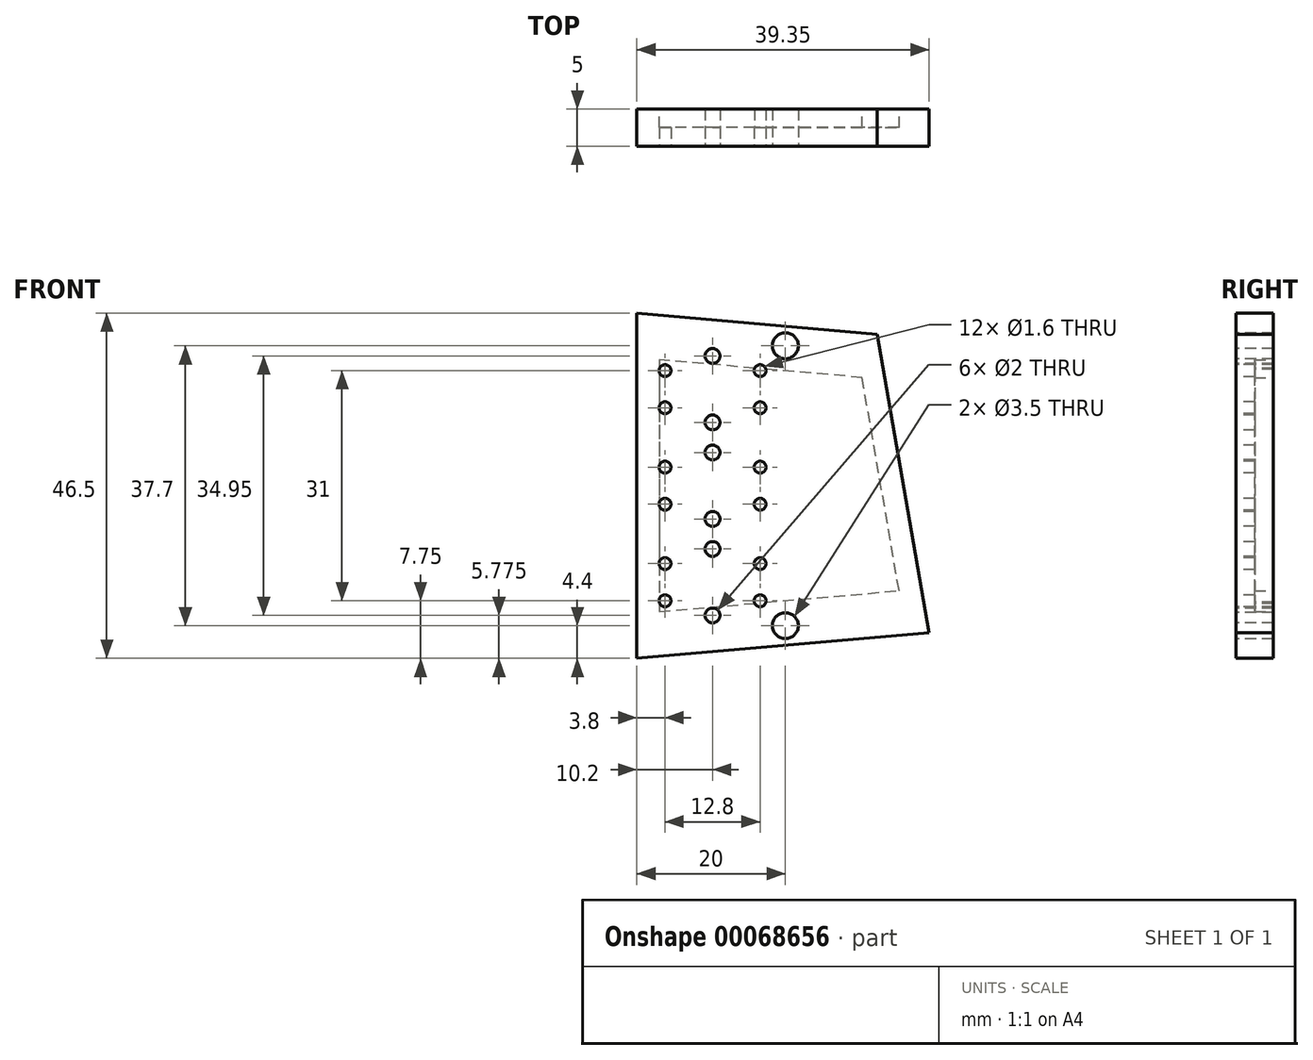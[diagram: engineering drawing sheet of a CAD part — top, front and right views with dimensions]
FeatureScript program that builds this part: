
annotation { "Feature Type Name" : "Feature", "Feature Type Description" : "" }
export const myFeature = defineFeature(function(context is Context, id is Id, definition is map)
    precondition{}
    {
        {
            var Q0;
            Q0=qCreatedBy(makeId("Front.planeOp"),FACE);
            var sketch = newSketch(context, id + "F0", { "sketchPlane" : qUnion([Q0])});
            skLineSegment(sketch, "E0", {"start": v(0, 46.5) * mm, "end": v(0, 0) * mm});
            skLineSegment(sketch, "E1", {"start": v(0, 0) * mm, "end": v(39.35, 3.44) * mm});
            skLineSegment(sketch, "E2", {"start": v(0, 46.5) * mm, "end": v(32.38, 43.67) * mm});
            skLineSegment(sketch, "E3", {"start": v(39.35, 3.44) * mm, "end": v(32.38, 43.67) * mm});
            skSolve(sketch);
        }
        {
            var Q0;
            Q0=makeQuery(id+"F0.imprint","IMPRINT",FACE,{"disambiguationData":[TD([[makeQuery(id+"F0.imprint","IMPRINT",EDGE,{"derivedFrom":sQuery(id+"F0.wireOp",EDGE,"E0")}),1.0]])]});
            extrude(context, id + "F1", {"entities" : qUnion([Q0]), "depth" : 5 * mm});
        }
        {
            var Q0;
            Q0=makeQuery(id+"F1.opExtrude","CAP_FACE",FACE,{"disambiguationData":[OSD([sQuery(id+"F0.wireOp",EDGE,"E0"),sQuery(id+"F0.wireOp",EDGE,"E1"),sQuery(id+"F0.wireOp",EDGE,"E2"),sQuery(id+"F0.wireOp",EDGE,"E3")])],"isStart":true});
            var sketch = newSketch(context, id + "F2", { "sketchPlane" : qUnion([Q0])});
            skLineSegment(sketch, "E4", {"start": v(-30.34, 37.82) * mm, "end": v(-3, 40.21) * mm});
            skLineSegment(sketch, "E5", {"start": v(-3, 40.21) * mm, "end": v(-3, 6.29) * mm});
            skLineSegment(sketch, "E6", {"start": v(-3, 6.29) * mm, "end": v(-35.32, 9.11) * mm});
            skLineSegment(sketch, "E7", {"start": v(-35.32, 9.11) * mm, "end": v(-30.34, 37.82) * mm});
            skSolve(sketch);
        }
        {
            var Q0;
            Q0=makeQuery(id+"F2.imprint","IMPRINT",FACE,{"disambiguationData":[TD([[makeQuery(id+"F2.imprint","IMPRINT",EDGE,{"derivedFrom":sQuery(id+"F2.wireOp",EDGE,"E4")}),-1.0]])]});
            extrude(context, id + "F3", {"entities" : qUnion([Q0]), "operationType" : NewBodyOperationType.REMOVE, "oppositeDirection" : true, "depth" : 2.5 * mm});
        }
        {
            var Q0;
            Q0=makeQuery(id+"F1.opExtrude","CAP_FACE",FACE,{"disambiguationData":[OSD([sQuery(id+"F0.wireOp",EDGE,"E0"),sQuery(id+"F0.wireOp",EDGE,"E1"),sQuery(id+"F0.wireOp",EDGE,"E2"),sQuery(id+"F0.wireOp",EDGE,"E3")])],"isStart":false});
            var sketch = newSketch(context, id + "F4", { "sketchPlane" : qUnion([Q0])});
            skPoint(sketch, "E8", {"position": v(0, 23.25) * mm});
            skLineSegment(sketch, "E9", {"start": v(0, 23.25) * mm, "end": v(35.92, 23.25) * mm, "construction": true});
            skLineSegment(sketch, "E10", {"start": v(16.6, 50) * mm, "end": v(16.6, 0) * mm, "construction": true});
            skLineSegment(sketch, "E11", {"start": v(3.8, 46.17) * mm, "end": v(3.8, 0) * mm, "construction": true});
            skLineSegment(sketch, "E12", {"start": v(0, 25.75) * mm, "end": v(35.48, 25.75) * mm, "construction": true});
            skLineSegment(sketch, "E13", {"start": v(0, 20.75) * mm, "end": v(36.35, 20.75) * mm, "construction": true});
            skLineSegment(sketch, "E14", {"start": v(20, 44.75) * mm, "end": v(20, 0) * mm, "construction": true});
            skPoint(sketch, "E15", {"position": v(20, 44.75) * mm});
            skPoint(sketch, "E16", {"position": v(20, 1.75) * mm});
            skPoint(sketch, "E17", {"position": v(20, 42.1) * mm});
            skPoint(sketch, "E18", {"position": v(20, 4.4) * mm});
            skPoint(sketch, "E19", {"position": v(3.8, 20.75) * mm});
            skPoint(sketch, "E20", {"position": v(3.8, 25.75) * mm});
            skPoint(sketch, "E21", {"position": v(16.6, 25.75) * mm});
            skPoint(sketch, "E22", {"position": v(16.6, 20.75) * mm});
            skPoint(sketch, "E23", {"position": v(3.8, 12.75) * mm});
            skPoint(sketch, "E24", {"position": v(3.8, 7.75) * mm});
            skPoint(sketch, "E25", {"position": v(3.8, 33.75) * mm});
            skPoint(sketch, "E26", {"position": v(3.8, 38.75) * mm});
            skPoint(sketch, "E27", {"position": v(16.6, 7.75) * mm});
            skPoint(sketch, "E28", {"position": v(16.6, 12.75) * mm});
            skPoint(sketch, "E29", {"position": v(16.6, 33.75) * mm});
            skPoint(sketch, "E30", {"position": v(16.6, 38.75) * mm});
            skLineSegment(sketch, "E31", {"start": v(5.78, 0) * mm, "end": v(5.78, 46) * mm, "construction": true});
            skLineSegment(sketch, "E32", {"start": v(14.63, 45.22) * mm, "end": v(14.63, 0) * mm, "construction": true});
            skLineSegment(sketch, "E33", {"start": v(0, 36.25) * mm, "end": v(33.66, 36.25) * mm, "construction": true});
            skLineSegment(sketch, "E34", {"start": v(0, 10.25) * mm, "end": v(38.17, 10.25) * mm, "construction": true});
            skPoint(sketch, "E35", {"position": v(5.78, 10.25) * mm});
            skPoint(sketch, "E36", {"position": v(14.63, 10.25) * mm});
            skPoint(sketch, "E37", {"position": v(5.78, 23.25) * mm});
            skPoint(sketch, "E38", {"position": v(14.63, 23.25) * mm});
            skPoint(sketch, "E39", {"position": v(5.78, 36.25) * mm});
            skPoint(sketch, "E40", {"position": v(14.63, 36.25) * mm});
            skLineSegment(sketch, "E41", {"start": v(10.2, 0) * mm, "end": v(10.2, 37.55) * mm, "construction": true});
            skPoint(sketch, "E42", {"position": v(10.2, 5.77) * mm});
            skPoint(sketch, "E43", {"position": v(10.2, 14.72) * mm});
            skPoint(sketch, "E44", {"position": v(10.2, 18.77) * mm});
            skPoint(sketch, "E45", {"position": v(10.2, 27.72) * mm});
            skPoint(sketch, "E46", {"position": v(10.2, 31.77) * mm});
            skPoint(sketch, "E47", {"position": v(10.2, 40.72) * mm});
            skPoint(sketch, "E48", {"position": v(10.2, 10.25) * mm});
            skPoint(sketch, "E49", {"position": v(10.2, 23.25) * mm});
            skPoint(sketch, "E50", {"position": v(10.2, 36.25) * mm});
            skLineSegment(sketch, "E51", {"start": v(0, 0) * mm, "end": v(39.35, 0) * mm, "construction": true});
            skLineSegment(sketch, "E52", {"start": v(39.35, 3.44) * mm, "end": v(39.35, 0) * mm, "construction": true});
            skSolve(sketch);
        }
        {
            var Q0;
            Q0=sQuery(id+"F4.wireOp",VERTEX,"E18");
            var Q1;
            Q1=sQuery(id+"F4.wireOp",VERTEX,"E17");
            var Q2;
            Q2=makeQuery(id+"F1.opExtrude","SWEPT_BODY",BODY,{"disambiguationData":[OSD([sQuery(id+"F0.wireOp",EDGE,"E0"),sQuery(id+"F0.wireOp",EDGE,"E1"),sQuery(id+"F0.wireOp",EDGE,"E2"),sQuery(id+"F0.wireOp",EDGE,"E3")])]});
            hole(context, id + "F5", {"style" : HoleStyle.SIMPLE, "holeDiameter" : 3.5 * mm, "endStyle" : HoleEndStyle.THROUGH, "locations" : qUnion([Q0, Q1]), "scope" : qUnion([Q2])});
        }
        {
            var Q0;
            Q0=sQuery(id+"F4.wireOp",VERTEX,"E24");
            var Q1;
            Q1=sQuery(id+"F4.wireOp",VERTEX,"E23");
            var Q2;
            Q2=sQuery(id+"F4.wireOp",VERTEX,"E19");
            var Q3;
            Q3=sQuery(id+"F4.wireOp",VERTEX,"E20");
            var Q4;
            Q4=sQuery(id+"F4.wireOp",VERTEX,"E25");
            var Q5;
            Q5=sQuery(id+"F4.wireOp",VERTEX,"E26");
            var Q6;
            Q6=sQuery(id+"F4.wireOp",VERTEX,"E30");
            var Q7;
            Q7=sQuery(id+"F4.wireOp",VERTEX,"E29");
            var Q8;
            Q8=sQuery(id+"F4.wireOp",VERTEX,"E21");
            var Q9;
            Q9=sQuery(id+"F4.wireOp",VERTEX,"E22");
            var Q10;
            Q10=sQuery(id+"F4.wireOp",VERTEX,"E28");
            var Q11;
            Q11=sQuery(id+"F4.wireOp",VERTEX,"E27");
            var Q12;
            Q12=makeQuery(id+"F1.opExtrude","SWEPT_BODY",BODY,{"disambiguationData":[OSD([sQuery(id+"F0.wireOp",EDGE,"E0"),sQuery(id+"F0.wireOp",EDGE,"E1"),sQuery(id+"F0.wireOp",EDGE,"E2"),sQuery(id+"F0.wireOp",EDGE,"E3")])]});
            hole(context, id + "F6", {"style" : HoleStyle.SIMPLE, "holeDiameter" : 1.6 * mm, "endStyle" : HoleEndStyle.THROUGH, "locations" : qUnion([Q0, Q1, Q2, Q3, Q4, Q5, Q6, Q7, Q8, Q9, Q10, Q11]), "scope" : qUnion([Q12])});
        }
        {
            var Q0;
            Q0=sQuery(id+"F4.wireOp",VERTEX,"E42");
            var Q1;
            Q1=sQuery(id+"F4.wireOp",VERTEX,"E43");
            var Q2;
            Q2=sQuery(id+"F4.wireOp",VERTEX,"E44");
            var Q3;
            Q3=sQuery(id+"F4.wireOp",VERTEX,"E45");
            var Q4;
            Q4=sQuery(id+"F4.wireOp",VERTEX,"E46");
            var Q5;
            Q5=sQuery(id+"F4.wireOp",VERTEX,"E47");
            var Q6;
            Q6=makeQuery(id+"F1.opExtrude","SWEPT_BODY",BODY,{"disambiguationData":[OSD([sQuery(id+"F0.wireOp",EDGE,"E0"),sQuery(id+"F0.wireOp",EDGE,"E1"),sQuery(id+"F0.wireOp",EDGE,"E2"),sQuery(id+"F0.wireOp",EDGE,"E3")])]});
            hole(context, id + "F7", {"style" : HoleStyle.SIMPLE, "holeDiameter" : 2 * mm, "endStyle" : HoleEndStyle.THROUGH, "locations" : qUnion([Q0, Q1, Q2, Q3, Q4, Q5]), "scope" : qUnion([Q6])});
        }
    });
